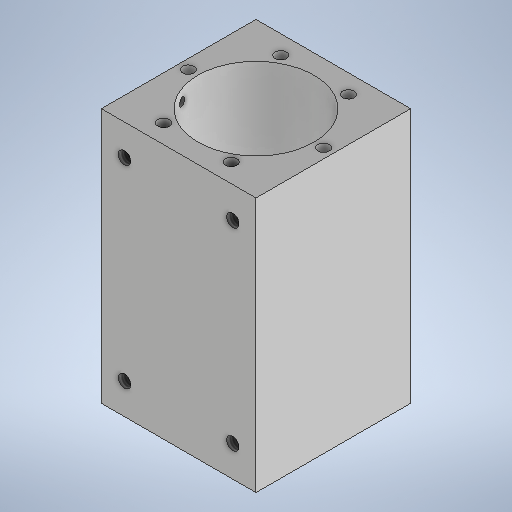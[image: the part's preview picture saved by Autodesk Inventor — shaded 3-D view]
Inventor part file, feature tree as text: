
AUTODESK INVENTOR PART (.ipt)
format: ipt  version: 2025.1 (Build 291241000, 241)  size: 442,368 bytes
history: native  units: mm
features: sketch x8, extrude x5, hole x5, mirror x2, fillet x2, thread x1, pattern_circular x1, plane x1, projected_geometry x1
ambient origin geometry x8: Origin, YZ Plane, XZ Plane, XY Plane, X Axis, Y Axis, Z Axis, Center Point
bodies: Solid1 (feature_tree)
feature tree (26):
  extrude  "Extrusion1"  Depth=40.0mm
  sketch  "Sketch2"  dims[d2=66.0mm d3=0.0mm d4=30.0mm]
  extrude  "Extrusion2"  Depth=66.0mm
  extrude  "Extrusion3"  Depth=66.0mm TaperAngle=0.0deg
  thread  "Thread3"  [1 undecoded]
  pattern_circular  "Circular Pattern2"  Count=6 Angle=360.0deg
  extrude  "Extrusion4"  Depth=32.0mm
  sketch  "Sketch4"  dims[d19=3.0mm d20=32.0mm]
  hole  "Hole1"  [1 undecoded]
  hole  "Hole2"  [1 undecoded]
  mirror  "Mirror1"
  extrude  "Extrusion5"  Depth=8.0mm
  fillet  "Fillet1"  Radius=30.0mm
  fillet  "Fillet2"  Radius=60.0mm
  hole  "Hole3"  [1 undecoded]
  hole  "Hole4"  [1 undecoded]
  hole  "Hole5"  [1 undecoded]
  plane  "Work Plane1"
  mirror  "Mirror2"
  sketch  "Sketch1"  dims[d0=40.0mm d1=40.0mm]
  sketch  "Sketch3"  dims[d5=35.0mm d7=66.0mm d8=0.0mm d9=10.0mm d10=0.0mm d16=60.0mm d17=360.0deg]
  sketch  "Sketch5"  dims[d21=2.0mm d22=4.0mm]
  projected_geometry  "Projected Loop1"
  sketch  "Sketch6"  dims[d23=8.0mm d24=3.5mm d25=0.0mm]
  sketch  "Sketch7"  dims[d28=8.0mm d29=9.0mm d30=30.0mm d31=60.0mm]
  sketch  "Sketch8"  dims[d32=18.0mm d33=9.0mm d34=2.013mm d35=8.0mm d36=4.0mm d37=2.0mm d38=90.0deg d39=8.0mm d40=0.0mm d41=2.013mm d42=8.0mm d43=4.0mm d44=2.0mm d45=90.0deg d46=8.0mm d47=0.0mm d48=4.0mm d49=4.0mm d52=4.0mm d53=4.0mm d54=4.0mm d55=3.0mm d56=8.0mm d57=4.5mm d58=0.0mm d59=1.0mm d60=1.0mm d61=30.0deg d62=3.0mm d68=8.0mm d69=0.0mm d70=29.5mm d71=59.0mm d72=15.0mm d73=30.0mm d74=2.459mm d75=6.0mm d76=4.0mm d77=2.0mm d78=90.0deg d79=8.8mm d80=0.0mm d81=2.013mm d82=5.0mm d83=4.0mm d84=2.0mm d85=90.0deg d86=5.0mm d87=0.0mm d88=16.0mm d89=8.0mm d90=50.0mm d91=28.0mm d92=3.242mm d93=8.0mm d94=4.0mm d95=2.0mm d96=90.0deg d97=8.0mm d98=0.0mm d99=-33.0mm]
note: 6 required parameter values undecoded (feature->parameter linkage not recoverable at this tier; creation-order binding heuristic only, values carry confidence <= 0.55)
